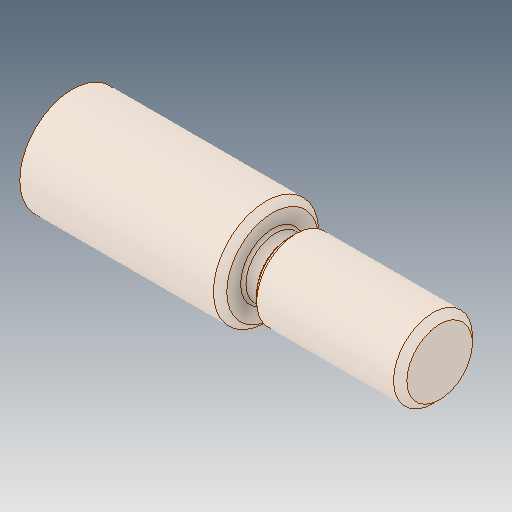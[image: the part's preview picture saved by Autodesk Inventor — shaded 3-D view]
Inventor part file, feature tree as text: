
AUTODESK INVENTOR PART (.ipt)
format: ipt  version: 2019 (Build 230136000, 136)  size: 128,512 bytes
history: native  units: mm
features: fillet x1
ambient origin geometry x8: Origin, YZ Plane, XZ Plane, XY Plane, X Axis, Y Axis, Z Axis, Center Point
bodies: Solid1 (feature_tree)
feature tree (1):
  fillet  "Fillet1"  [1 undecoded]
note: 1 required parameter value undecoded (feature->parameter linkage not recoverable at this tier; creation-order binding heuristic only, values carry confidence <= 0.55)
